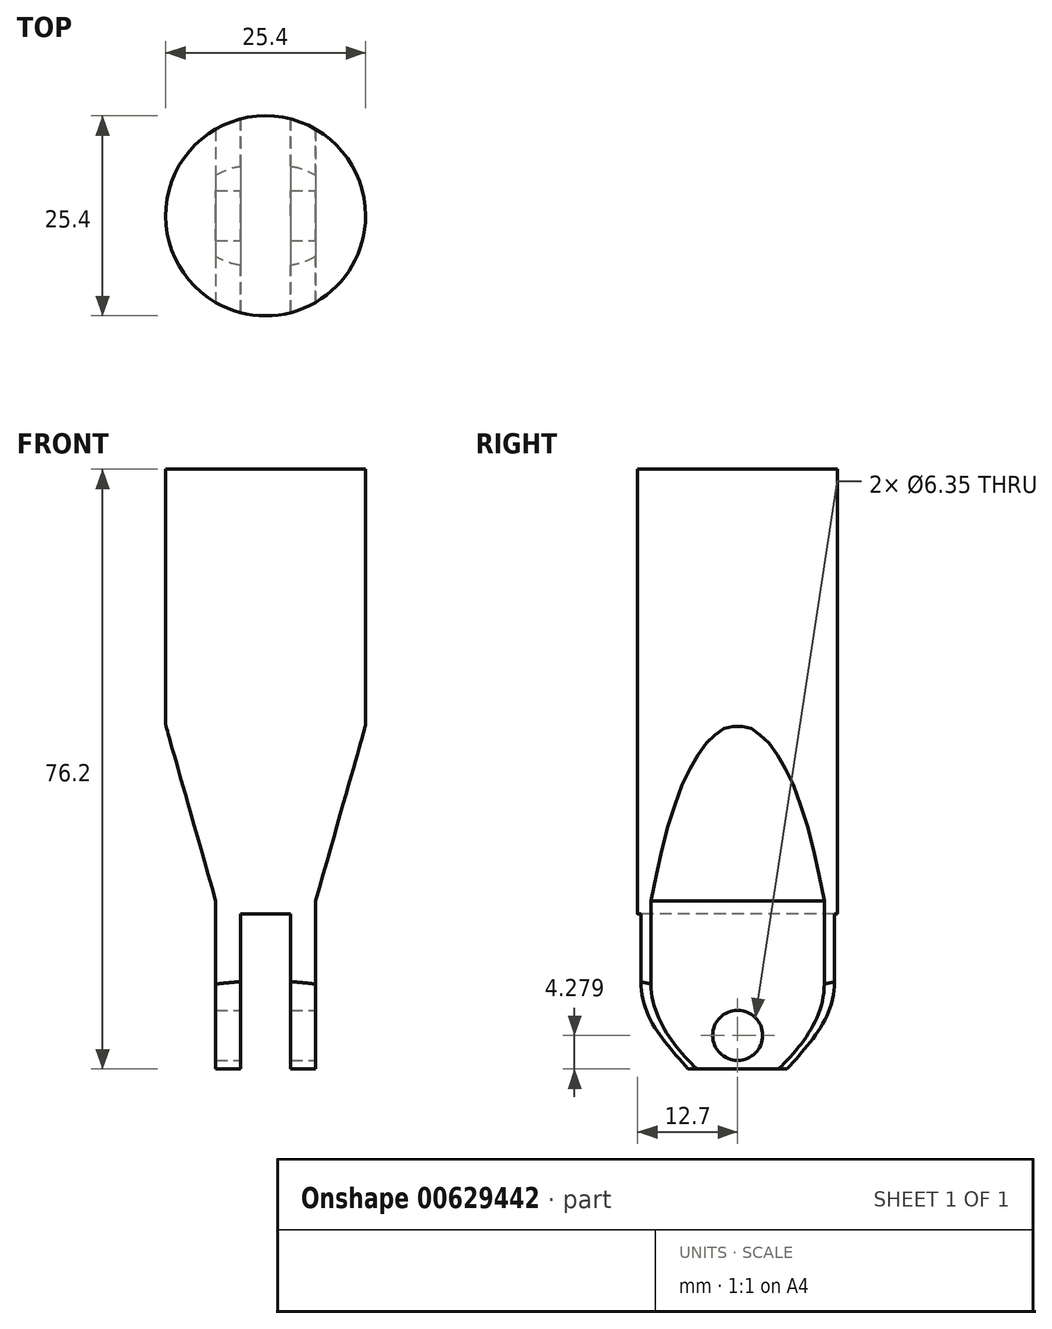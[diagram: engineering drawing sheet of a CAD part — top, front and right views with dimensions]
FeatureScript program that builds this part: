
annotation { "Feature Type Name" : "Feature", "Feature Type Description" : "" }
export const myFeature = defineFeature(function(context is Context, id is Id, definition is map)
    precondition{}
    {
        {
            var Q0;
            Q0=qCreatedBy(makeId("Top.planeOp"),FACE);
            var sketch = newSketch(context, id + "F0", { "sketchPlane" : qUnion([Q0])});
            skCircle(sketch, "E0", {"center": v(0, 0) * mm, "radius": 12.7 * mm});
            skSolve(sketch);
        }
        {
            var Q0;
            Q0=makeQuery(id+"F0.imprint","IMPRINT",FACE,{"disambiguationData":[TD([[makeQuery(id+"F0.imprint","IMPRINT",EDGE,{"derivedFrom":sQuery(id+"F0.wireOp",EDGE,"E0")}),1.0]])]});
            extrude(context, id + "F1", {"entities" : qUnion([Q0]), "depth" : 101.6 * mm, "offsetDistance" : 25.4 * mm});
        }
        {
            var Q0;
            Q0=qCreatedBy(makeId("Front.planeOp"),FACE);
            var sketch = newSketch(context, id + "F2", { "sketchPlane" : qUnion([Q0])});
            skLineSegment(sketch, "E1.bottom", {"start": v(6.35, 21.33) * mm, "end": v(-6.35, 21.33) * mm});
            skLineSegment(sketch, "E1.top", {"start": v(6.35, -21.33) * mm, "end": v(-6.35, -21.33) * mm});
            skLineSegment(sketch, "E1.left", {"start": v(6.35, 21.33) * mm, "end": v(6.35, -21.33) * mm});
            skLineSegment(sketch, "E1.right", {"start": v(-6.35, 21.33) * mm, "end": v(-6.35, -21.33) * mm});
            skPoint(sketch, "E1.middle", {"position": v(0, 0) * mm});
            skLineSegment(sketch, "E2", {"start": v(-6.35, 21.33) * mm, "end": v(-34.84, 121.71) * mm});
            skLineSegment(sketch, "E3", {"start": v(-34.84, 121.71) * mm, "end": v(-34.84, -20.22) * mm});
            skLineSegment(sketch, "E4", {"start": v(-34.84, -20.22) * mm, "end": v(-6.35, -20.22) * mm});
            skLineSegment(sketch, "E5.MirrorCS", {"start": v(6.35, 21.33) * mm, "end": v(34.84, 121.71) * mm});
            skLineSegment(sketch, "E6.MirrorCS", {"start": v(34.84, 121.71) * mm, "end": v(34.84, -20.22) * mm});
            skLineSegment(sketch, "E7.MirrorCS", {"start": v(34.84, -20.22) * mm, "end": v(6.35, -20.22) * mm});
            skSolve(sketch);
        }
        {
            var Q0;
            {var subQ0=sQuery(id+"F2.wireOp",EDGE,"E2");Q0=makeQuery(id+"F2.imprint","IMPRINT",FACE,{"disambiguationData":[TD([[makeQuery(id+"F2.imprint","IMPRINT",EDGE,{"derivedFrom":subQ0}),1.0]])]});}
            var Q1;
            {var subQ0=sQuery(id+"F2.wireOp",EDGE,"E5.MirrorCS");Q1=makeQuery(id+"F2.imprint","IMPRINT",FACE,{"disambiguationData":[TD([[makeQuery(id+"F2.imprint","IMPRINT",EDGE,{"derivedFrom":subQ0}),-1.0]])]});}
            extrude(context, id + "F3", {"entities" : qUnion([Q0, Q1]), "operationType" : NewBodyOperationType.REMOVE, "oppositeDirection" : true, "depth" : 25.4 * mm, "offsetDistance" : 25.4 * mm, "symmetric" : true});
        }
        {
            var Q0;
            Q0=qCreatedBy(makeId("Right.planeOp"),FACE);
            var sketch = newSketch(context, id + "F4", { "sketchPlane" : qUnion([Q0])});
            skLineSegment(sketch, "E8", {"start": v(0, 0) * mm, "end": v(6.35, 0) * mm});
            skLineSegment(sketch, "E9", {"start": v(6.35, 0) * mm, "end": v(21.4, 17.65) * mm});
            skLineSegment(sketch, "E10", {"start": v(21.4, 17.65) * mm, "end": v(17.69, -33.11) * mm});
            skLineSegment(sketch, "E11", {"start": v(17.69, -33.11) * mm, "end": v(6.35, 0) * mm});
            skLineSegment(sketch, "E12.MirrorCS", {"start": v(-17.69, -33.11) * mm, "end": v(-6.35, 0) * mm});
            skLineSegment(sketch, "E13.MirrorCS", {"start": v(-6.35, 0) * mm, "end": v(-21.4, 17.65) * mm});
            skLineSegment(sketch, "E14.MirrorCS", {"start": v(-21.4, 17.65) * mm, "end": v(-17.69, -33.11) * mm});
            skSolve(sketch);
        }
        {
            var Q0;
            Q0=makeQuery(id+"F4.imprint","IMPRINT",FACE,{"disambiguationData":[TD([[makeQuery(id+"F4.imprint","IMPRINT",EDGE,{"derivedFrom":sQuery(id+"F4.wireOp",EDGE,"E9")}),-1.0]])]});
            var Q1;
            Q1=makeQuery(id+"F4.imprint","IMPRINT",FACE,{"disambiguationData":[TD([[makeQuery(id+"F4.imprint","IMPRINT",EDGE,{"derivedFrom":sQuery(id+"F4.wireOp",EDGE,"E12.MirrorCS")}),1.0]])]});
            extrude(context, id + "F5", {"entities" : qUnion([Q0, Q1]), "operationType" : NewBodyOperationType.REMOVE, "oppositeDirection" : true, "depth" : 25.4 * mm, "offsetDistance" : 25.4 * mm, "symmetric" : true});
        }
        {
            var Q0;
            Q0=makeQuery(id+"F5.boolean.opBoolean","INTERSECT",EDGE,{"derivedFrom":[makeQuery(id+"F1.opExtrude","SWEPT_FACE",FACE,{"disambiguationData":[OSD([sQuery(id+"F0.wireOp",EDGE,"E0")])]}),makeQuery(id+"F5.opExtrude","SWEPT_FACE",FACE,{"disambiguationData":[OSD([sQuery(id+"F4.wireOp",EDGE,"E13.MirrorCS")])]})]});
            var Q1;
            Q1=makeQuery(id+"F5.boolean.opBoolean","COPY",EDGE,{"derivedFrom":makeQuery(id+"F5.opExtrude","SWEPT_EDGE",EDGE,{"disambiguationData":[OSD([sQuery(id+"F4.wireOp",EDGE,"E12.MirrorCS"),sQuery(id+"F4.wireOp",EDGE,"E13.MirrorCS")])]})});
            var Q2;
            Q2=makeQuery(id+"F5.boolean.opBoolean","COPY",EDGE,{"derivedFrom":makeQuery(id+"F5.opExtrude","SWEPT_EDGE",EDGE,{"disambiguationData":[OSD([sQuery(id+"F4.wireOp",EDGE,"E9"),sQuery(id+"F4.wireOp",EDGE,"E11")])]})});
            var Q3;
            Q3=makeQuery(id+"F5.boolean.opBoolean","INTERSECT",EDGE,{"derivedFrom":[makeQuery(id+"F1.opExtrude","SWEPT_FACE",FACE,{"disambiguationData":[OSD([sQuery(id+"F0.wireOp",EDGE,"E0")])]}),makeQuery(id+"F5.opExtrude","SWEPT_FACE",FACE,{"disambiguationData":[OSD([sQuery(id+"F4.wireOp",EDGE,"E9")])]})]});
            fillet(context, id + "F6", {"entities" : qUnion([Q0, Q1, Q2, Q3]), "radius" : 10.16 * mm, "tangentPropagation" : true, "allowEdgeOverflow" : false});
        }
        {
            var Q0;
            Q0=qCreatedBy(makeId("Front.planeOp"),FACE);
            var sketch = newSketch(context, id + "F7", { "sketchPlane" : qUnion([Q0])});
            skPoint(sketch, "E15.middle", {"position": v(0, 0) * mm});
            skPoint(sketch, "E15.left.start.orphan", {"position": v(-3.17, 32.73) * mm});
            skPoint(sketch, "E15.right.start.orphan", {"position": v(3.18, 32.73) * mm});
            skPoint(sketch, "E15.top.end.orphan", {"position": v(3.17, -32.73) * mm});
            skPoint(sketch, "E15.top.start.orphan", {"position": v(-3.18, -32.73) * mm});
            skLineSegment(sketch, "E16.bottom", {"start": v(-3.17, 19.7) * mm, "end": v(3.18, 19.7) * mm});
            skLineSegment(sketch, "E16.top", {"start": v(-3.18, -19.7) * mm, "end": v(3.17, -19.7) * mm});
            skLineSegment(sketch, "E16.left", {"start": v(-3.17, 19.7) * mm, "end": v(-3.18, -19.7) * mm});
            skLineSegment(sketch, "E16.right", {"start": v(3.18, 19.7) * mm, "end": v(3.17, -19.7) * mm});
            skSolve(sketch);
        }
        {
            var Q0;
            Q0 = qSketchRegion(id + "F7", true);
            extrude(context, id + "F8", {"entities" : qUnion([Q0]), "operationType" : NewBodyOperationType.REMOVE, "oppositeDirection" : true, "depth" : 25.4 * mm, "offsetDistance" : 25.4 * mm, "symmetric" : true});
        }
        {
            var Q0;
            Q0=makeQuery(id+"F3.boolean.opBoolean","COPY",FACE,{"derivedFrom":makeQuery(id+"F3.opExtrude","SWEPT_FACE",FACE,{"disambiguationData":[OSD([sQuery(id+"F2.wireOp",EDGE,"E1.left")])]})});
            var sketch = newSketch(context, id + "F9", { "sketchPlane" : qUnion([Q0])});
            skCircle(sketch, "E17", {"center": v(0, 4.28) * mm, "radius": 3.18 * mm});
            skSolve(sketch);
        }
        {
            var Q0;
            Q0 = qSketchRegion(id + "F9", true);
            extrude(context, id + "F10", {"entities" : qUnion([Q0]), "operationType" : NewBodyOperationType.REMOVE, "oppositeDirection" : true, "depth" : 25.4 * mm, "offsetDistance" : 25.4 * mm});
        }
        {
            var Q0;
            Q0=makeQuery(id+"F1.opExtrude","CAP_FACE",FACE,{"disambiguationData":[OSD([sQuery(id+"F0.wireOp",EDGE,"E0")])],"isStart":false});
            extrude(context, id + "F11", {"entities" : qUnion([Q0]), "operationType" : NewBodyOperationType.REMOVE, "oppositeDirection" : true, "depth" : 25.4 * mm, "offsetDistance" : 25.4 * mm});
        }
    });
